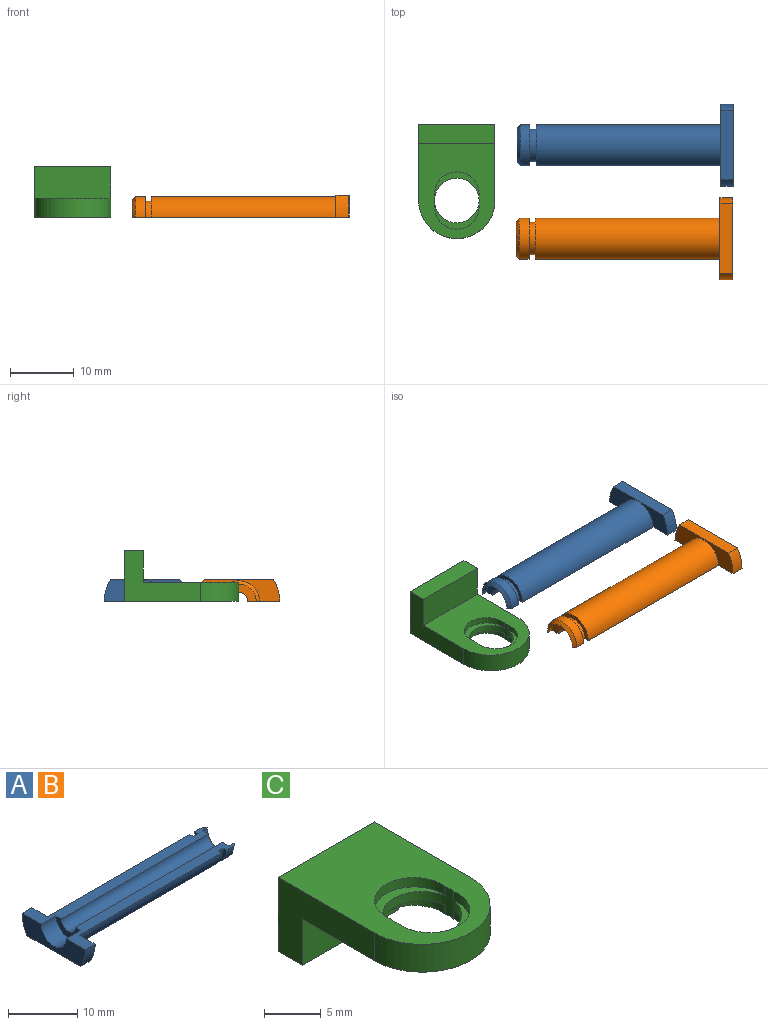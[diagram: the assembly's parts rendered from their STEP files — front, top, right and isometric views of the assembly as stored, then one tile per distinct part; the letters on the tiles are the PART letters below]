
ASSEMBLY  parts=3 mates=2
PART A: 18 faces, bbox 34x12.9x3.5 mm
  f0: cylinder r=3.25mm len=29mm, axis (-1,0,0), area 296.1mm2, adj f1,f4,f8,f16
  f1: plane 34x5mm, normal (0,0,1), area 62.2mm2, adj f0,f2,f3,f5,f8,f9,f10,f11
  f2: cylinder r=1.45mm len=30mm, axis (-1,0,0), area 136.7mm2, adj f1,f4,f10,f12
  f3: cylinder r=3.25mm len=6.5mm, axis (-1,0,0), area 15.3mm2, adj f1,f4,f11,f15
  f4: plane 34x5mm, normal (0,0,1), area 62.2mm2, adj f0,f2,f3,f7,f8,f9,f10,f11
  f5: cylinder r=6.45mm len=3.45mm, axis (-1,0,0), area 7.3mm2, adj f1,f6,f8,f17
  f6: plane 10.9x2mm, normal (0,0,-1), area 21.8mm2, adj f5,f7,f8,f17
  f7: cylinder r=6.45mm len=3.45mm, axis (-1,0,0), area 7.3mm2, adj f4,f6,f8,f17
  f8: plane 12.9x3.45mm, normal (1,0,0), area 25.7mm2, adj f0,f1,f4,f5,f6,f7
  f9: cylinder r=2.55mm len=5.1mm, axis (-1,0,0), area 24mm2, adj f1,f4,f10,f17
  f10: plane 5.1x2.55mm, normal (-1,0,0), area 6.9mm2, adj f1,f2,f4,f9
  f11: cone r=2.75mm half-angle=45deg, axis (-1,0,0), area 6.7mm2, adj f1,f3,f4,f13
  f12: plane 5.5x2.75mm, normal (1,0,0), area 8.6mm2, adj f1,f2,f4,f13
  f13: cylinder r=2.75mm len=5.5mm, axis (1,0,0), area 8.6mm2, adj f1,f4,f11,f12
  f14: cylinder r=2.55mm len=5.1mm, axis (-1,0,0), area 8mm2, adj f1,f4,f15,f16
  f15: plane 6.5x3.25mm, normal (-1,0,0), area 6.4mm2, adj f1,f3,f4,f14
  f16: plane 6.5x3.25mm, normal (1,0,0), area 6.4mm2, adj f0,f1,f4,f14
  f17: plane 12.9x3.45mm, normal (-1,0,0), area 32.1mm2, adj f1,f4,f5,f6,f7,f9
PART B: same geometry as A
PART C: 17 faces, bbox 12x18x8 mm
  f0: plane 18x12mm, normal (0,0,1), area 148.1mm2, adj f2,f3,f4,f5,f12,f14,f16
  f1: plane 15x12mm, normal (0,0,-1), area 112.1mm2, adj f2,f3,f4,f5,f6,f8,f10
  f2: plane 12x8mm, normal (-1,0,0), area 51mm2, adj f0,f1,f3,f10,f11,f16
  f3: cylinder r=6mm len=12mm, axis (0,0,1), area 56.5mm2, adj f0,f1,f2,f4
  f4: plane 12x8mm, normal (1,0,0), area 51mm2, adj f0,f1,f3,f10,f11,f16
  f5: cylinder r=3.5mm len=7mm, axis (0,0,1), area 26mm2, adj f0,f1,f6,f7,f8,f9,f12,f13
  f6: cylinder r=3.5mm len=7mm, axis (0,0,-1), area 12mm2, adj f1,f5,f7
  f7: plane 7x4mm, normal (0,0,-1), area 7mm2, adj f5,f6
  f8: cylinder r=3.5mm len=7mm, axis (0,0,-1), area 12mm2, adj f1,f5,f9
  f9: plane 7x4mm, normal (0,0,-1), area 7mm2, adj f5,f8
  f10: plane 12x5mm, normal (0,-1,0), area 60mm2, adj f1,f2,f4,f11
  f11: plane 12x3mm, normal (0,0,-1), area 36mm2, adj f2,f4,f10,f16
  f12: cylinder r=3.5mm len=7mm, axis (0,0,1), area 12mm2, adj f0,f5,f13
  f13: plane 7x4mm, normal (0,0,1), area 7mm2, adj f5,f12
  f14: cylinder r=3.5mm len=7mm, axis (0,0,1), area 12mm2, adj f0,f5,f15
  f15: plane 7x4mm, normal (0,0,1), area 7mm2, adj f5,f14
  f16: plane 12x8mm, normal (0,1,0), area 96mm2, adj f0,f2,f4,f11
PLACE A rot(axis=(0,-1,0),180deg) t=(21.88,20.38,-5.36)mm
PLACE B rot(axis=(0,-1,0),180deg) t=(21.76,5.7,-5.36)mm
PLACE C rot(axis=(0,-1,0),180deg) t=(-36.4,11.7,-5.36)mm
MATE planar C.f0 <-> A.f1  axis (0,0,-1) through (-14.59,17.7,-5.36)mm
MATE planar C.f0 <-> B.f1  axis (0,0,-1) through (-14.59,17.7,-5.36)mm
